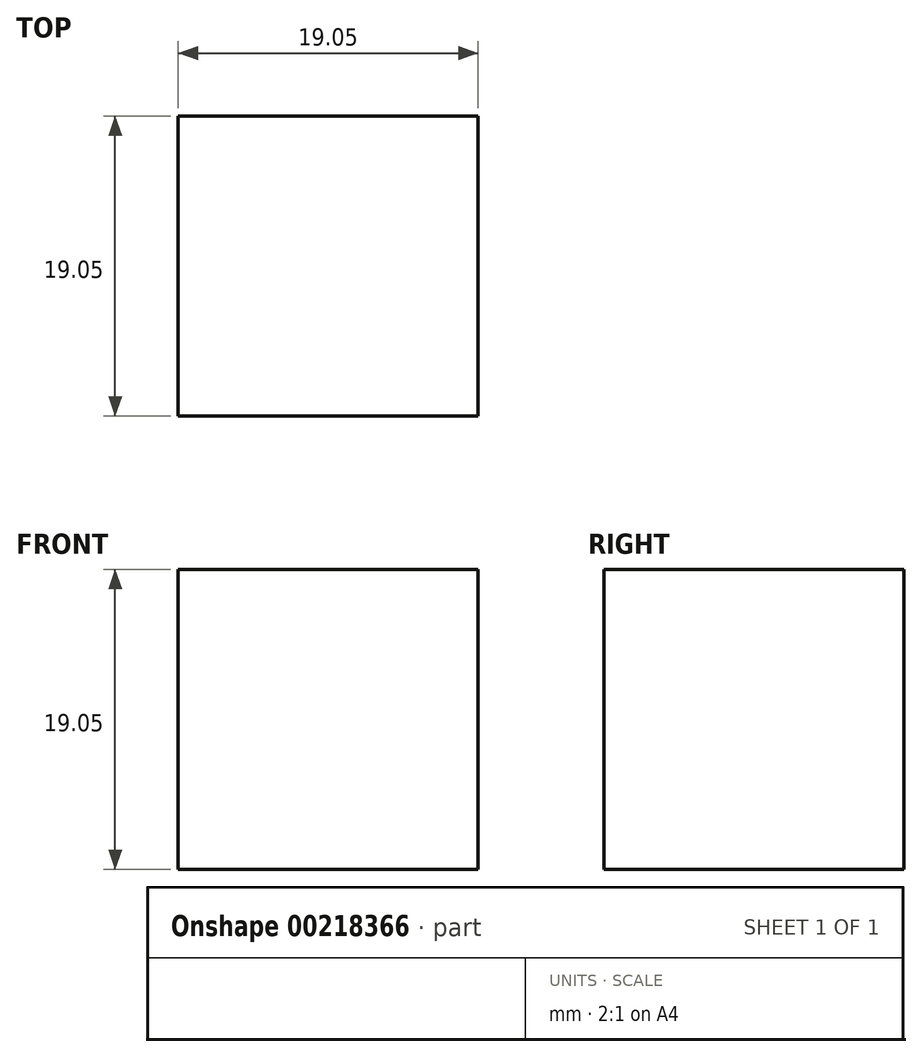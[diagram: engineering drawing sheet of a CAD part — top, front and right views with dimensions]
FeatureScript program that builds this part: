
annotation { "Feature Type Name" : "Feature", "Feature Type Description" : "" }
export const myFeature = defineFeature(function(context is Context, id is Id, definition is map)
    precondition{}
    {
        {
            var Q0;
            Q0=qCreatedBy(makeId("Front.planeOp"),FACE);
            var sketch = newSketch(context, id + "F0", { "sketchPlane" : qUnion([Q0])});
            skLineSegment(sketch, "E0.bottom", {"start": v(-37.88, 36.04) * mm, "end": v(-18.83, 36.04) * mm});
            skLineSegment(sketch, "E0.top", {"start": v(-37.88, 17) * mm, "end": v(-18.83, 17) * mm});
            skLineSegment(sketch, "E0.left", {"start": v(-37.88, 36.04) * mm, "end": v(-37.88, 17) * mm});
            skLineSegment(sketch, "E0.right", {"start": v(-18.83, 36.04) * mm, "end": v(-18.83, 17) * mm});
            skSolve(sketch);
        }
        {
            var Q0;
            Q0=makeQuery(id+"F0.imprint","IMPRINT",FACE,{"disambiguationData":[TD([[makeQuery(id+"F0.imprint","IMPRINT",EDGE,{"derivedFrom":sQuery(id+"F0.wireOp",EDGE,"E0.bottom")}),-1.0]])]});
            extrude(context, id + "F1", {"entities" : qUnion([Q0]), "depth" : 19.05 * mm});
        }
    });
